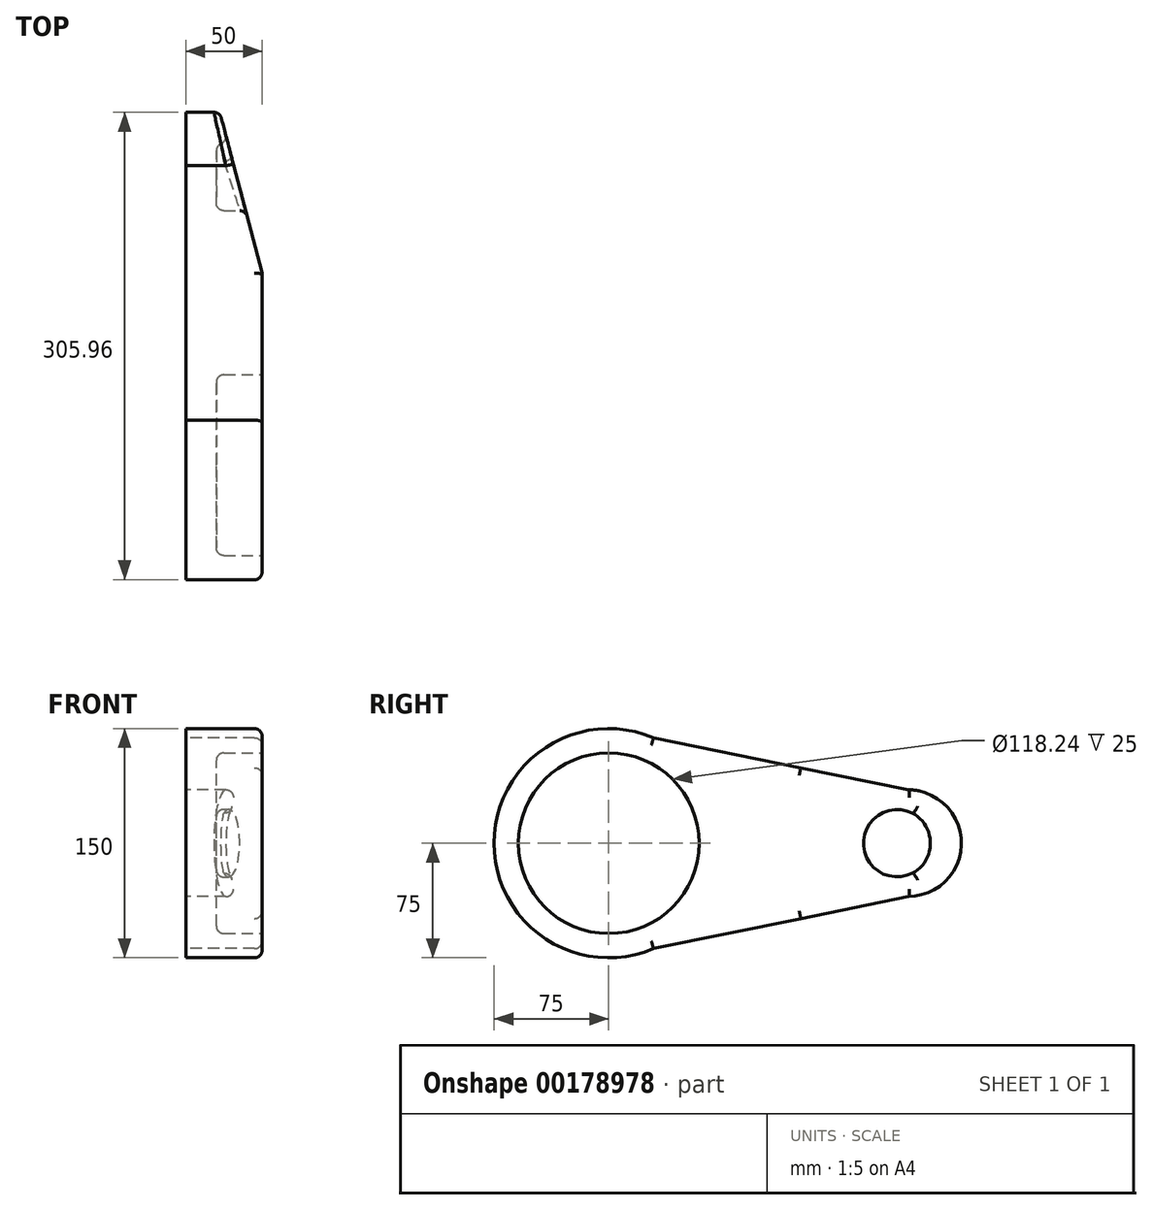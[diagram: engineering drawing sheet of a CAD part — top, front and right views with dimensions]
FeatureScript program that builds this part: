
annotation { "Feature Type Name" : "Feature", "Feature Type Description" : "" }
export const myFeature = defineFeature(function(context is Context, id is Id, definition is map)
    precondition{}
    {
        {
            var Q0;
            Q0=qCreatedBy(makeId("Right.planeOp"),FACE);
            var sketch = newSketch(context, id + "F0", { "sketchPlane" : qUnion([Q0])});
            skCircle(sketch, "E0", {"center": v(0, 0) * mm, "radius": 75 * mm});
            skCircle(sketch, "E1", {"center": v(195.96, 0) * mm, "radius": 35 * mm});
            skLineSegment(sketch, "E2", {"start": v(195.96, 35) * mm, "end": v(0, 75) * mm});
            skLineSegment(sketch, "E3", {"start": v(0, -75) * mm, "end": v(195.96, -35) * mm});
            skSolve(sketch);
        }
        {
            var Q0;
            Q0 = qSketchRegion(id + "F0", true);
            var Q1;
            {var subQ0=sQuery(id+"F0.wireOp",EDGE,"E1");var subQ1=makeQuery(id+"F0.imprint","INTERSECT",VERTEX,{"derivedFrom":[subQ0,sQuery(id+"F0.wireOp",EDGE,"E2")]});Q1=makeQuery(id+"F0.imprint","IMPRINT",FACE,{"disambiguationData":[TD([[makeQuery(id+"F0.imprint","IMPRINT",EDGE,{"disambiguationData":[TD([[subQ1,-1.0]])],"derivedFrom":subQ0}),1.0]])]});}
            extrude(context, id + "F1", {"entities" : qUnion([Q0, Q1]), "depth" : 50 * mm});
        }
        {
            var Q0;
            Q0=makeQuery(id+"F1.opExtrude","CAP_FACE",FACE,{"disambiguationData":[OSD([sQuery(id+"F0.wireOp",EDGE,"E0"),sQuery(id+"F0.wireOp",EDGE,"E1"),sQuery(id+"F0.wireOp",EDGE,"E2"),sQuery(id+"F0.wireOp",EDGE,"E3")])],"isStart":false});
            var sketch = newSketch(context, id + "F2", { "sketchPlane" : qUnion([Q0])});
            skSolve(sketch);
        }
        {
            var Q0;
            Q0=makeQuery(id+"F2.imprint","IMPRINT",FACE,{"disambiguationData":[TD([[makeQuery(id+"F2.imprint","IMPRINT",EDGE,{"derivedFrom":makeQuery(id+"F1.opExtrude","CAP_EDGE",EDGE,{"disambiguationData":[OSD([sQuery(id+"F0.wireOp",EDGE,"E0")])],"isStart":false})}),1.0]])]});
            var sketch = newSketch(context, id + "F3", { "sketchPlane" : qUnion([Q0])});
            skCircle(sketch, "E4", {"center": v(0, 0) * mm, "radius": 59.12 * mm});
            skCircle(sketch, "E5", {"center": v(188.7, 0) * mm, "radius": 22.12 * mm});
            skPoint(sketch, "E6", {"position": v(111.69, 0) * mm});
            skSolve(sketch);
        }
        {
            var Q0;
            Q0=makeQuery(id+"F3.imprint","IMPRINT",FACE,{"disambiguationData":[TD([[makeQuery(id+"F3.imprint","IMPRINT",EDGE,{"derivedFrom":sQuery(id+"F3.wireOp",EDGE,"E4")}),1.0]])]});
            var Q1;
            Q1=makeQuery(id+"F3.imprint","IMPRINT",FACE,{"disambiguationData":[TD([[makeQuery(id+"F3.imprint","IMPRINT",EDGE,{"derivedFrom":sQuery(id+"F3.wireOp",EDGE,"E5")}),1.0]])]});
            var Q2;
            Q2=sQuery(id+"F3.wireOp",EDGE,"E4");
            var Q3;
            Q3=sQuery(id+"F3.wireOp",EDGE,"E5");
            extrude(context, id + "F4", {"entities" : qUnion([Q0, Q1]), "operationType" : NewBodyOperationType.REMOVE, "surfaceEntities" : qUnion([Q2, Q3]), "oppositeDirection" : true, "depth" : 30 * mm});
        }
        {
            var Q0;
            Q0=makeQuery(id+"F4.boolean.opBoolean","COPY",EDGE,{"derivedFrom":makeQuery(id+"F4.opExtrude","CAP_EDGE",EDGE,{"disambiguationData":[OSD([sQuery(id+"F3.wireOp",EDGE,"E4")])],"isStart":true})});
            var Q1;
            Q1=makeQuery(id+"F4.boolean.opBoolean","COPY",FACE,{"derivedFrom":makeQuery(id+"F4.opExtrude","SWEPT_FACE",FACE,{"disambiguationData":[OSD([sQuery(id+"F3.wireOp",EDGE,"E5")])]})});
            var Q2;
            Q2=makeQuery(id+"F4.boolean.opBoolean","COPY",EDGE,{"derivedFrom":makeQuery(id+"F4.opExtrude","CAP_EDGE",EDGE,{"disambiguationData":[OSD([sQuery(id+"F3.wireOp",EDGE,"E5")])],"isStart":true})});
            var Q3;
            Q3=makeQuery(id+"F1.opExtrude","CAP_EDGE",EDGE,{"disambiguationData":[OSD([sQuery(id+"F0.wireOp",EDGE,"E3")])],"isStart":false});
            var Q4;
            Q4=makeQuery(id+"F1.opExtrude","CAP_EDGE",EDGE,{"disambiguationData":[OSD([sQuery(id+"F0.wireOp",EDGE,"E2")])],"isStart":false});
            var Q5;
            Q5=makeQuery(id+"F1.opExtrude","CAP_EDGE",EDGE,{"disambiguationData":[OSD([sQuery(id+"F0.wireOp",EDGE,"E0")])],"isStart":false});
            var Q6;
            Q6=makeQuery(id+"F1.opExtrude","CAP_EDGE",EDGE,{"disambiguationData":[OSD([sQuery(id+"F0.wireOp",EDGE,"E1")])],"isStart":false});
            fillet(context, id + "F5", {"entities" : qUnion([Q0, Q1, Q2, Q3, Q4, Q5, Q6]), "radius" : 5 * mm, "tangentPropagation" : true, "allowEdgeOverflow" : false});
        }
        {
            var Q0;
            {var subQ0=sQuery(id+"F3.wireOp",EDGE,"E5");Q0=makeQuery(id+"F5.opFillet","BLEND_EDGE",EDGE,{"blendedFrom":[makeQuery(id+"F4.boolean.opBoolean","COPY",EDGE,{"derivedFrom":makeQuery(id+"F4.opExtrude","CAP_EDGE",EDGE,{"disambiguationData":[OSD([subQ0])],"isStart":false})}),makeQuery(id+"F4.boolean.opBoolean","COPY",FACE,{"derivedFrom":makeQuery(id+"F4.opExtrude","SWEPT_FACE",FACE,{"disambiguationData":[OSD([subQ0])]})})],"blendedInto":[makeQuery(id+"F4.boolean.opBoolean","COPY",FACE,{"derivedFrom":makeQuery(id+"F4.opExtrude","SWEPT_FACE",FACE,{"disambiguationData":[OSD([subQ0])]})})]});}
            var Q1;
            Q1=makeQuery(id+"F4.boolean.opBoolean","COPY",EDGE,{"derivedFrom":makeQuery(id+"F4.opExtrude","CAP_EDGE",EDGE,{"disambiguationData":[OSD([sQuery(id+"F3.wireOp",EDGE,"E4")])],"isStart":false})});
            fillet(context, id + "F6", {"entities" : qUnion([Q0, Q1]), "radius" : 5 * mm, "tangentPropagation" : true, "allowEdgeOverflow" : false});
        }
        {
            var Q0;
            Q0=qCreatedBy(makeId("Top.planeOp"),FACE);
            var sketch = newSketch(context, id + "F7", { "sketchPlane" : qUnion([Q0])});
            skLineSegment(sketch, "E7", {"start": v(53.8, 110.84) * mm, "end": v(20.4, 238.22) * mm});
            skLineSegment(sketch, "E8", {"start": v(53.8, 110.84) * mm, "end": v(53.8, 238.58) * mm});
            skLineSegment(sketch, "E9", {"start": v(53.8, 238.58) * mm, "end": v(20.4, 238.22) * mm});
            skSolve(sketch);
        }
        {
            var Q0;
            Q0 = qSketchRegion(id + "F7", true);
            var Q1;
            Q1=makeQuery(id+"F7.imprint","IMPRINT",FACE,{"disambiguationData":[TD([[makeQuery(id+"F7.imprint","IMPRINT",EDGE,{"derivedFrom":sQuery(id+"F7.wireOp",EDGE,"E7")}),-1.0]])]});
            extrude(context, id + "F8", {"entities" : qUnion([Q0, Q1]), "operationType" : NewBodyOperationType.REMOVE, "oppositeDirection" : true, "depth" : 80 * mm, "hasSecondDirection" : true, "secondDirectionOppositeDirection" : false, "secondDirectionDepth" : 80 * mm});
        }
        {
            var Q0;
            Q0=makeQuery(id+"F8.boolean.opBoolean","INTERSECT",EDGE,{"derivedFrom":[makeQuery(id+"F1.opExtrude","CAP_FACE",FACE,{"disambiguationData":[OSD([sQuery(id+"F0.wireOp",EDGE,"E0"),sQuery(id+"F0.wireOp",EDGE,"E1"),sQuery(id+"F0.wireOp",EDGE,"E2"),sQuery(id+"F0.wireOp",EDGE,"E3")])],"isStart":false}),makeQuery(id+"F8.opExtrude","SWEPT_FACE",FACE,{"disambiguationData":[OSD([sQuery(id+"F7.wireOp",EDGE,"E7")])]})]});
            var Q1;
            Q1=makeQuery(id+"F8.boolean.opBoolean","INTERSECT",EDGE,{"derivedFrom":[makeQuery(id+"F1.opExtrude","CAP_FACE",FACE,{"disambiguationData":[OSD([sQuery(id+"F0.wireOp",EDGE,"E0"),sQuery(id+"F0.wireOp",EDGE,"E1"),sQuery(id+"F0.wireOp",EDGE,"E2"),sQuery(id+"F0.wireOp",EDGE,"E3")])],"isStart":false}),makeQuery(id+"F8.opExtrude","SWEPT_FACE",FACE,{"disambiguationData":[OSD([sQuery(id+"F7.wireOp",EDGE,"E7")])]})]});
            var Q2;
            Q2=makeQuery(id+"F8.boolean.opBoolean","INTERSECT",EDGE,{"derivedFrom":[makeQuery(id+"F1.opExtrude","SWEPT_FACE",FACE,{"disambiguationData":[OSD([sQuery(id+"F0.wireOp",EDGE,"E1")])]}),makeQuery(id+"F8.opExtrude","SWEPT_FACE",FACE,{"disambiguationData":[OSD([sQuery(id+"F7.wireOp",EDGE,"E7")])]})]});
            var Q3;
            {var subQ0=sQuery(id+"F3.wireOp",EDGE,"E5");Q3=makeQuery(id+"F5.opFillet","BLEND_EDGE",EDGE,{"blendedFrom":[makeQuery(id+"F4.boolean.opBoolean","COPY",EDGE,{"derivedFrom":makeQuery(id+"F4.opExtrude","CAP_EDGE",EDGE,{"disambiguationData":[OSD([subQ0])],"isStart":false})}),makeQuery(id+"F4.boolean.opBoolean","COPY",FACE,{"derivedFrom":makeQuery(id+"F4.opExtrude","SWEPT_FACE",FACE,{"disambiguationData":[OSD([subQ0])]})})],"blendedInto":[makeQuery(id+"F4.boolean.opBoolean","COPY",FACE,{"derivedFrom":makeQuery(id+"F4.opExtrude","SWEPT_FACE",FACE,{"disambiguationData":[OSD([subQ0])]})})]});}
            var Q4;
            {var subQ0=sQuery(id+"F3.wireOp",EDGE,"E5");Q4=makeQuery(id+"F5.opFillet","BLEND_EDGE",EDGE,{"blendedFrom":[makeQuery(id+"F4.boolean.opBoolean","COPY",EDGE,{"derivedFrom":makeQuery(id+"F4.opExtrude","CAP_EDGE",EDGE,{"disambiguationData":[OSD([subQ0])],"isStart":false})}),makeQuery(id+"F4.boolean.opBoolean","COPY",FACE,{"derivedFrom":makeQuery(id+"F4.opExtrude","CAP_FACE",FACE,{"disambiguationData":[OSD([subQ0])],"isStart":false})})],"blendedInto":[makeQuery(id+"F4.boolean.opBoolean","COPY",FACE,{"derivedFrom":makeQuery(id+"F4.opExtrude","CAP_FACE",FACE,{"disambiguationData":[OSD([subQ0])],"isStart":false})})]});}
            var Q5;
            Q5=makeQuery(id+"F8.boolean.opBoolean","INTERSECT",EDGE,{"derivedFrom":[makeQuery(id+"F4.boolean.opBoolean","COPY",FACE,{"derivedFrom":makeQuery(id+"F4.opExtrude","SWEPT_FACE",FACE,{"disambiguationData":[OSD([sQuery(id+"F3.wireOp",EDGE,"E5")])]})}),makeQuery(id+"F8.opExtrude","SWEPT_FACE",FACE,{"disambiguationData":[OSD([sQuery(id+"F7.wireOp",EDGE,"E7")])]})]});
            fillet(context, id + "F9", {"entities" : qUnion([Q0, Q1, Q2, Q3, Q4, Q5]), "radius" : 5 * mm, "tangentPropagation" : true, "allowEdgeOverflow" : false});
        }
    });
